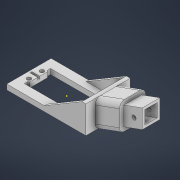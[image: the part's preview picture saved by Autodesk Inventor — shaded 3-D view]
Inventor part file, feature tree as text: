
AUTODESK INVENTOR PART (.ipt)
format: ipt  version: 2021 (Build 250183000, 183)  size: 425,472 bytes
history: native  units: mm
features: extrude x13, sketch x11, shell x1, fillet x1
ambient origin geometry x8: Origin, YZ Plane, XZ Plane, XY Plane, X Axis, Y Axis, Z Axis, Center Point
bodies: Body1 (feature_tree)
feature tree (26):
  extrude  "Extrusion2"  Depth=20.2mm
  extrude  "Extrusion3"  Depth=7.0mm
  sketch  "Skizze3"  dims[d9=4.0mm d10=0.0mm d11=3.2mm]
  extrude  "Extrusion4"  Depth=4.0mm
  extrude  "Extrusion5"  Depth=10.0mm
  sketch  "Skizze4"  dims[d12=3.2mm d15=10.0mm]
  extrude  "Extrusion6"  Depth=4.0mm TaperAngle=0.0deg
  sketch  "Skizze6"  dims[d16=5.0mm d17=4.0mm d18=0.0mm]
  extrude  "Extrusion7"  Depth=1.5mm
  extrude  "Extrusion9"  Depth=7.0mm
  shell  "Wandung2"  Thickness=2.0mm
  fillet  "Rundung1"  Radius=3.0mm
  extrude  "Extrusion10"  Depth=20.0mm
  extrude  "Extrusion11"  Depth=21.216mm
  extrude  "Extrusion12"  Depth=20.0mm TaperAngle=0.0deg
  extrude  "Extrusion14"  Depth=10.0mm
  extrude  "Extrusion15"  Depth=18.0mm
  extrude  "Extrusion13"  Depth=10.0mm
  sketch  "Skizze1"  dims[d0=41.0mm d3=20.2mm]
  sketch  "Skizze2"  dims[d7=58.0mm d8=7.0mm]
  sketch  "Skizze7"  dims[d19=7.0mm d20=1.5mm]
  sketch  "Skizze8"  dims[d21=2.0mm d22=0.0mm d23=7.0mm d24=2.0mm d25=0.0mm d26=3.0mm]
  sketch  "Skizze9"  dims[d27=21.216mm d28=20.0mm]
  sketch  "Skizze10"  dims[d29=21.216mm d30=3.490659mm]
  sketch  "Skizze11"  dims[d31=34.2mm d32=0.0mm d33=20.0mm d34=0.0mm]
  sketch  "Skizze12"  dims[d36=4.0mm d38=19.198622mm d42=18.0mm d44=19.198622mm d48=14.314467mm d51=13.5mm d52=0.0mm d53=2.0mm d54=2.0mm d55=0.0mm d56=2.0mm d57=0.0mm d60=3.2mm d62=27.925268mm d63=8.0mm d64=10.0mm d65=0.0mm d66=14.5mm d67=27.925268mm d68=50.0mm d69=0.0mm d70=5.0mm d71=5.0mm d81=2.0mm d82=1.0mm d83=9.434881mm d84=14.107462mm d85=10.0mm d86=0.0mm d87=40.0mm d88=0.0mm]
